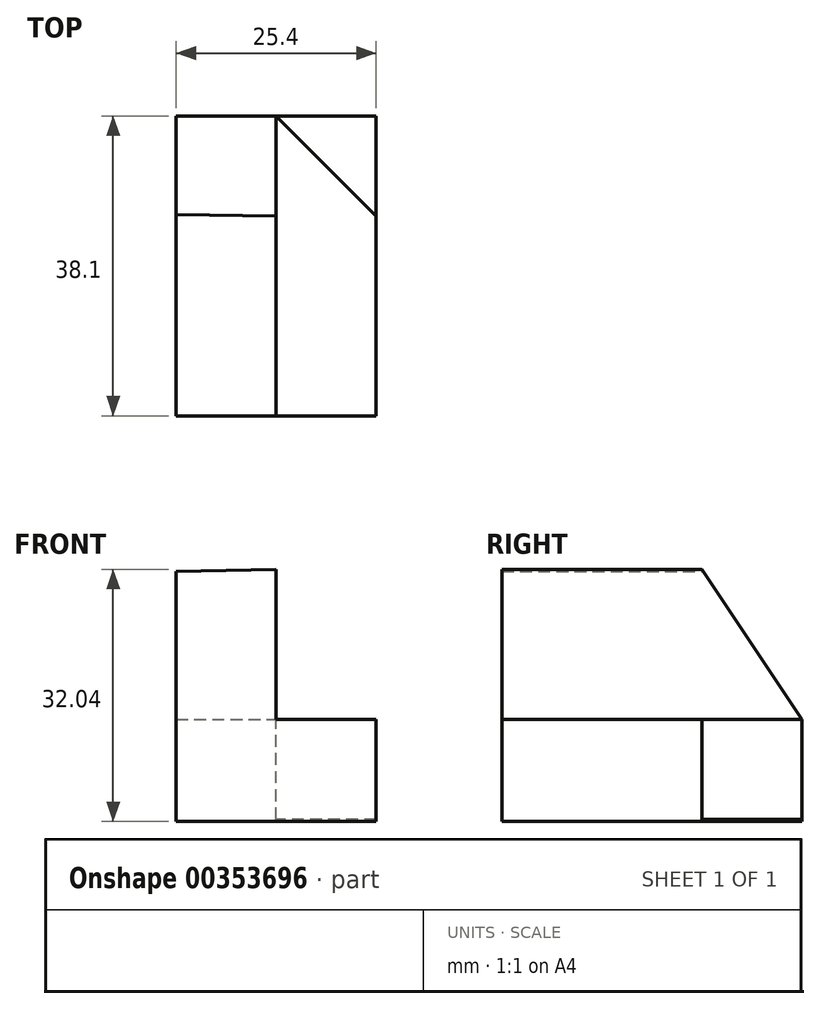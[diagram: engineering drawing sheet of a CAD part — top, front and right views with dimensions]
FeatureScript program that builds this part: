
annotation { "Feature Type Name" : "Feature", "Feature Type Description" : "" }
export const myFeature = defineFeature(function(context is Context, id is Id, definition is map)
    precondition{}
    {
        {
            var Q0;
            Q0=qCreatedBy(makeId("Front.planeOp"),FACE);
            var sketch = newSketch(context, id + "F0", { "sketchPlane" : qUnion([Q0])});
            skLineSegment(sketch, "E0", {"start": v(13.22, 43) * mm, "end": v(13.22, 11.25) * mm});
            skLineSegment(sketch, "E1", {"start": v(13.22, 11.25) * mm, "end": v(38.62, 11.25) * mm});
            skLineSegment(sketch, "E2", {"start": v(38.62, 11.25) * mm, "end": v(38.62, 24.24) * mm});
            skLineSegment(sketch, "E3", {"start": v(38.62, 24.24) * mm, "end": v(25.92, 24.24) * mm});
            skLineSegment(sketch, "E4", {"start": v(25.92, 24.24) * mm, "end": v(25.92, 43.3) * mm});
            skLineSegment(sketch, "E5", {"start": v(25.92, 43.3) * mm, "end": v(13.22, 43) * mm});
            skSolve(sketch);
        }
        {
            var Q0;
            Q0=makeQuery(id+"F0.imprint","IMPRINT",FACE,{"disambiguationData":[TD([[makeQuery(id+"F0.imprint","IMPRINT",EDGE,{"derivedFrom":sQuery(id+"F0.wireOp",EDGE,"E0")}),1.0]])]});
            extrude(context, id + "F1", {"entities" : qUnion([Q0]), "depth" : 38.1 * mm});
        }
        {
            var Q0;
            Q0=makeQuery(id+"F1.opExtrude","SWEPT_FACE",FACE,{"disambiguationData":[OSD([sQuery(id+"F0.wireOp",EDGE,"E4")])]});
            var sketch = newSketch(context, id + "F2", { "sketchPlane" : qUnion([Q0])});
            skLineSegment(sketch, "E6", {"start": v(0, 24.24) * mm, "end": v(-12.7, 43.3) * mm});
            skSolve(sketch);
        }
        {
            var Q0;
            Q0=makeQuery(id+"F1.opExtrude","SWEPT_FACE",FACE,{"disambiguationData":[OSD([sQuery(id+"F0.wireOp",EDGE,"E3")])]});
            var sketch = newSketch(context, id + "F3", { "sketchPlane" : qUnion([Q0])});
            skLineSegment(sketch, "E7", {"start": v(25.92, 0) * mm, "end": v(38.62, -12.7) * mm});
            skSolve(sketch);
        }
        {
            var Q0;
            {var subQ0=sQuery(id+"F3.wireOp",EDGE,"E7");Q0=makeQuery(id+"F3.imprint","IMPRINT",FACE,{"disambiguationData":[TD([[makeQuery(id+"F3.imprint","IMPRINT",EDGE,{"derivedFrom":subQ0}),1.0]])]});}
            extrude(context, id + "F4", {"entities" : qUnion([Q0]), "operationType" : NewBodyOperationType.REMOVE, "oppositeDirection" : true, "depth" : 12.7 * mm});
        }
        {
            var Q0;
            {var subQ0=sQuery(id+"F2.wireOp",EDGE,"E6");Q0=makeQuery(id+"F2.imprint","IMPRINT",FACE,{"disambiguationData":[TD([[makeQuery(id+"F2.imprint","IMPRINT",EDGE,{"derivedFrom":subQ0}),-1.0]])]});}
            extrude(context, id + "F5", {"entities" : qUnion([Q0]), "operationType" : NewBodyOperationType.REMOVE, "oppositeDirection" : true, "depth" : 12.7 * mm});
        }
    });
